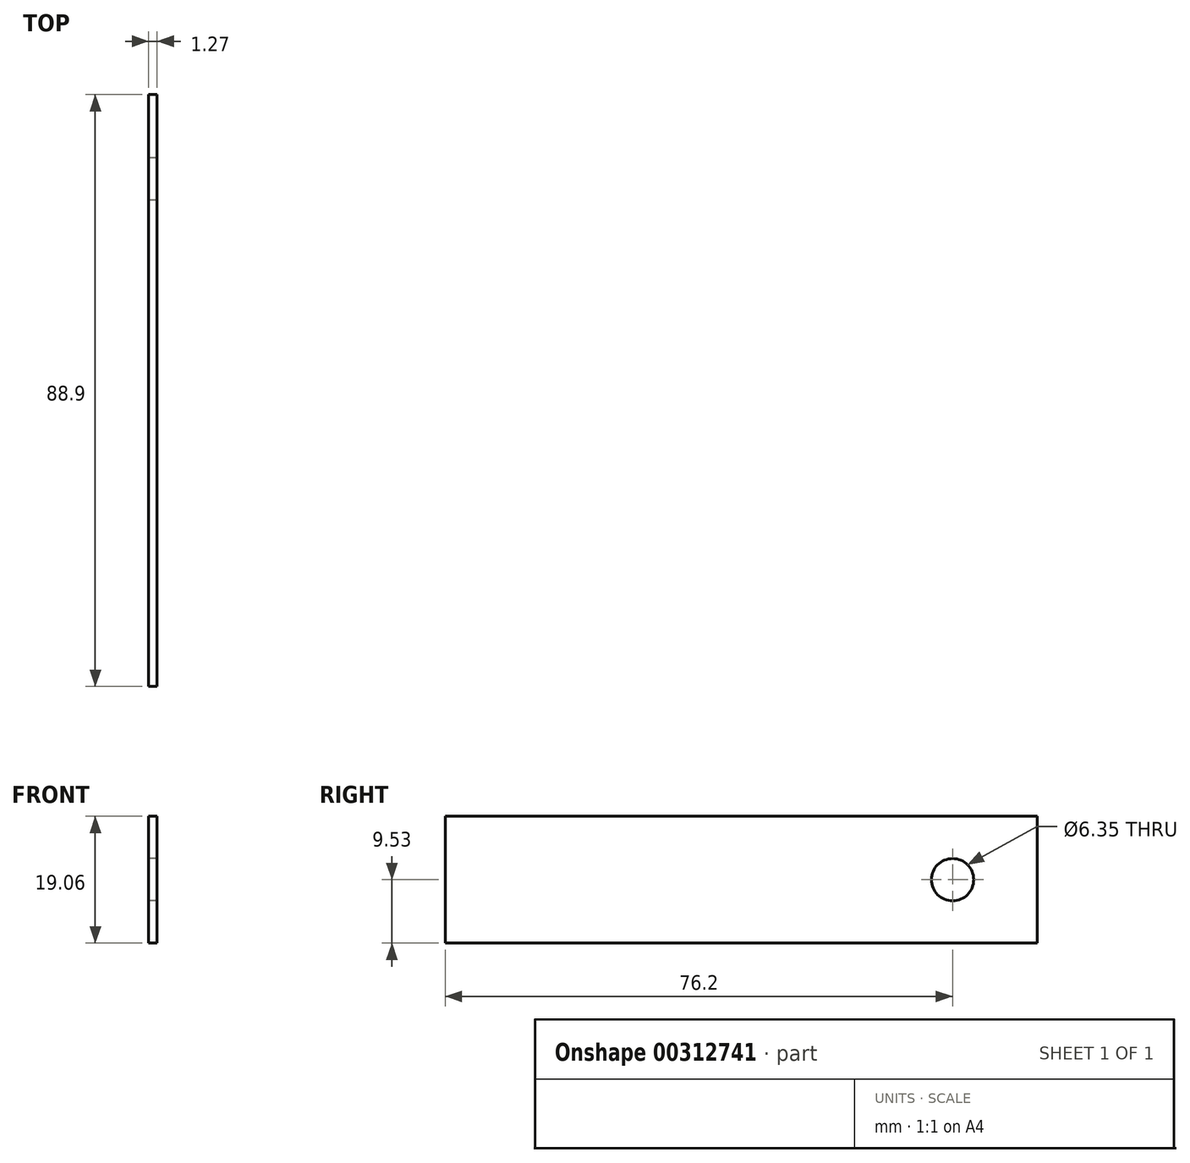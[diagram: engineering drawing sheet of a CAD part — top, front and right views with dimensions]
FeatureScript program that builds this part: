
annotation { "Feature Type Name" : "Feature", "Feature Type Description" : "" }
export const myFeature = defineFeature(function(context is Context, id is Id, definition is map)
    precondition{}
    {
        {
            var Q0;
            Q0=qCreatedBy(makeId("Right.planeOp"),FACE);
            var sketch = newSketch(context, id + "F0", { "sketchPlane" : qUnion([Q0])});
            skLineSegment(sketch, "E0.bottom", {"start": v(44.45, 9.53) * mm, "end": v(-44.45, 9.53) * mm});
            skLineSegment(sketch, "E0.top", {"start": v(44.45, -9.53) * mm, "end": v(-44.45, -9.53) * mm});
            skLineSegment(sketch, "E0.left", {"start": v(44.45, 9.53) * mm, "end": v(44.45, -9.53) * mm});
            skLineSegment(sketch, "E0.right", {"start": v(-44.45, 9.53) * mm, "end": v(-44.45, -9.53) * mm});
            skPoint(sketch, "E0.middle", {"position": v(0, 0) * mm});
            skCircle(sketch, "E1", {"center": v(31.75, 0) * mm, "radius": 3.18 * mm});
            skSolve(sketch);
        }
        {
            var Q0;
            Q0 = qSketchRegion(id + "F0", true);
            extrude(context, id + "F1", {"entities" : qUnion([Q0]), "depth" : 1.27 * mm});
        }
    });
